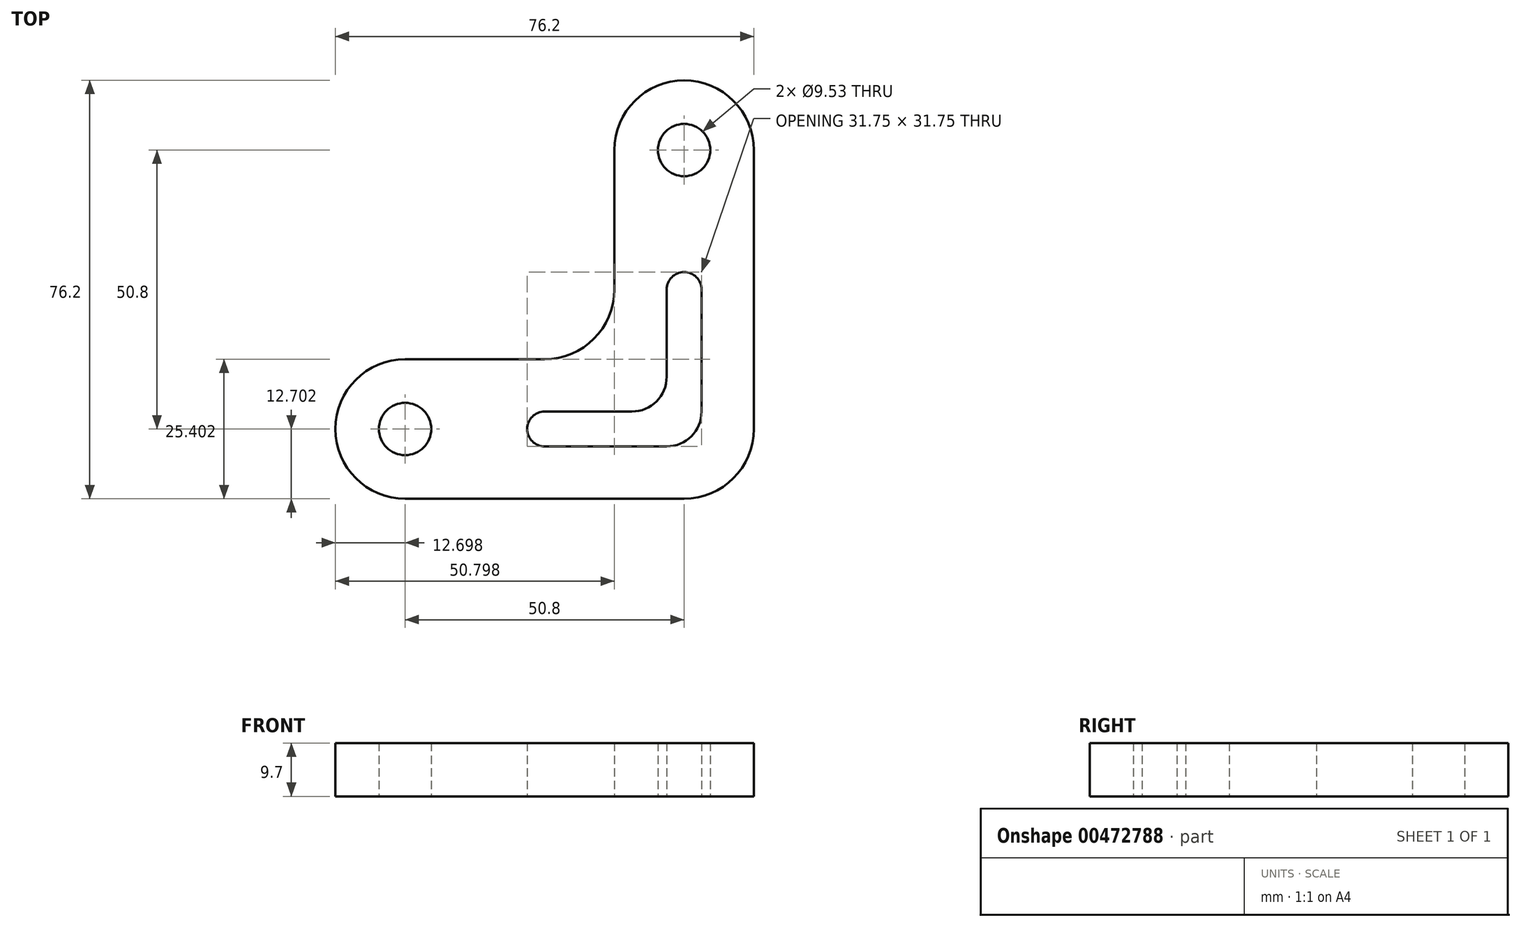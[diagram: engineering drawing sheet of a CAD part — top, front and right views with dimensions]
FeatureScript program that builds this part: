
annotation { "Feature Type Name" : "Feature", "Feature Type Description" : "" }
export const myFeature = defineFeature(function(context is Context, id is Id, definition is map)
    precondition{}
    {
        {
            var Q0;
            Q0=qCreatedBy(makeId("Top.planeOp"),FACE);
            var sketch = newSketch(context, id + "F0", { "sketchPlane" : qUnion([Q0])});
            skLineSegment(sketch, "E0.bottom", {"start": v(0, 0) * mm, "end": v(101.6, 0) * mm, "construction": true});
            skLineSegment(sketch, "E0.top", {"start": v(0, 101.6) * mm, "end": v(101.6, 101.6) * mm, "construction": true});
            skLineSegment(sketch, "E0.left", {"start": v(0, 0) * mm, "end": v(0, 101.6) * mm, "construction": true});
            skLineSegment(sketch, "E0.right", {"start": v(101.6, 0) * mm, "end": v(101.6, 101.6) * mm, "construction": true});
            skLineSegment(sketch, "E1", {"start": v(25.32, 22.86) * mm, "end": v(76.12, 22.86) * mm});
            skLineSegment(sketch, "E2", {"start": v(88.82, 35.56) * mm, "end": v(88.82, 86.36) * mm});
            skLineSegment(sketch, "E3", {"start": v(76.12, 99.06) * mm, "end": v(76.12, 99.06) * mm});
            skLineSegment(sketch, "E4", {"start": v(63.42, 86.36) * mm, "end": v(63.42, 60.96) * mm});
            skLineSegment(sketch, "E5", {"start": v(50.72, 48.26) * mm, "end": v(25.32, 48.26) * mm});
            skArc(sketch, "E6", {"start": v(25.32, 48.26) * mm, "mid": v(12.62, 35.56) * mm, "end": v(25.32, 22.86) * mm});
            skPoint(sketch, "E7.visualSharp", {"position": v(63.42, 99.06) * mm});
            skArc(sketch, "E7.filletArc", {"start": v(76.12, 99.06) * mm, "mid": v(67.14, 95.34) * mm, "end": v(63.42, 86.36) * mm});
            skPoint(sketch, "E8.visualSharp", {"position": v(88.82, 99.06) * mm});
            skArc(sketch, "E8.filletArc", {"start": v(88.82, 86.36) * mm, "mid": v(85.1, 95.34) * mm, "end": v(76.12, 99.06) * mm});
            skPoint(sketch, "E9.visualSharp", {"position": v(63.42, 48.26) * mm});
            skArc(sketch, "E9.filletArc", {"start": v(50.72, 48.26) * mm, "mid": v(59.7, 51.98) * mm, "end": v(63.42, 60.96) * mm});
            skPoint(sketch, "E10.visualSharp", {"position": v(88.82, 22.86) * mm});
            skArc(sketch, "E10.filletArc", {"start": v(76.12, 22.86) * mm, "mid": v(85.1, 26.58) * mm, "end": v(88.82, 35.56) * mm});
            skCircle(sketch, "E11", {"center": v(25.32, 35.56) * mm, "radius": 4.76 * mm});
            skCircle(sketch, "E12", {"center": v(76.12, 86.36) * mm, "radius": 4.76 * mm});
            skLineSegment(sketch, "E13.0", {"start": v(79.3, 38.74) * mm, "end": v(79.3, 60.96) * mm});
            skArc(sketch, "E13.1", {"start": v(76.12, 32.39) * mm, "mid": v(78.36, 33.32) * mm, "end": v(79.3, 35.56) * mm});
            skLineSegment(sketch, "E13.3", {"start": v(72.94, 86.36) * mm, "end": v(72.94, 82.81) * mm});
            skPoint(sketch, "E14.centerSnap0", {"position": v(79.3, 60.96) * mm});
            skArc(sketch, "E15", {"start": v(50.72, 38.74) * mm, "mid": v(47.54, 35.56) * mm, "end": v(50.72, 32.39) * mm});
            skLineSegment(sketch, "E16.trimOffspring", {"start": v(50.72, 32.39) * mm, "end": v(72.94, 32.39) * mm});
            skPoint(sketch, "E13.2.start.orphan", {"position": v(25.32, 32.39) * mm});
            skLineSegment(sketch, "E17.trimOffspring", {"start": v(79.3, 82.81) * mm, "end": v(79.3, 86.36) * mm});
            skPoint(sketch, "E14.center.orphan", {"position": v(76.04, 60.96) * mm});
            skArc(sketch, "E18", {"start": v(79.3, 60.96) * mm, "mid": v(76.12, 64.14) * mm, "end": v(72.94, 60.96) * mm});
            skPoint(sketch, "E19.newPointA", {"position": v(79.3, 35.56) * mm});
            skPoint(sketch, "E19.newPointB", {"position": v(76.12, 32.39) * mm});
            skLineSegment(sketch, "E20", {"start": v(50.72, 38.74) * mm, "end": v(66.6, 38.74) * mm});
            skLineSegment(sketch, "E21", {"start": v(72.94, 60.96) * mm, "end": v(72.94, 45.09) * mm});
            skArc(sketch, "E22.filletArc", {"start": v(66.6, 38.74) * mm, "mid": v(71.08, 40.6) * mm, "end": v(72.94, 45.09) * mm});
            skArc(sketch, "E23.filletArc", {"start": v(72.94, 32.39) * mm, "mid": v(77.43, 34.25) * mm, "end": v(79.3, 38.74) * mm});
            skSolve(sketch);
        }
        {
            var Q0;
            Q0=makeQuery(id+"F0.imprint","IMPRINT",FACE,{"disambiguationData":[TD([[makeQuery(id+"F0.imprint","IMPRINT",EDGE,{"derivedFrom":sQuery(id+"F0.wireOp",EDGE,"E1")}),1.0]])]});
            extrude(context, id + "F1", {"entities" : qUnion([Q0]), "depth" : 9.7 * mm});
        }
    });
